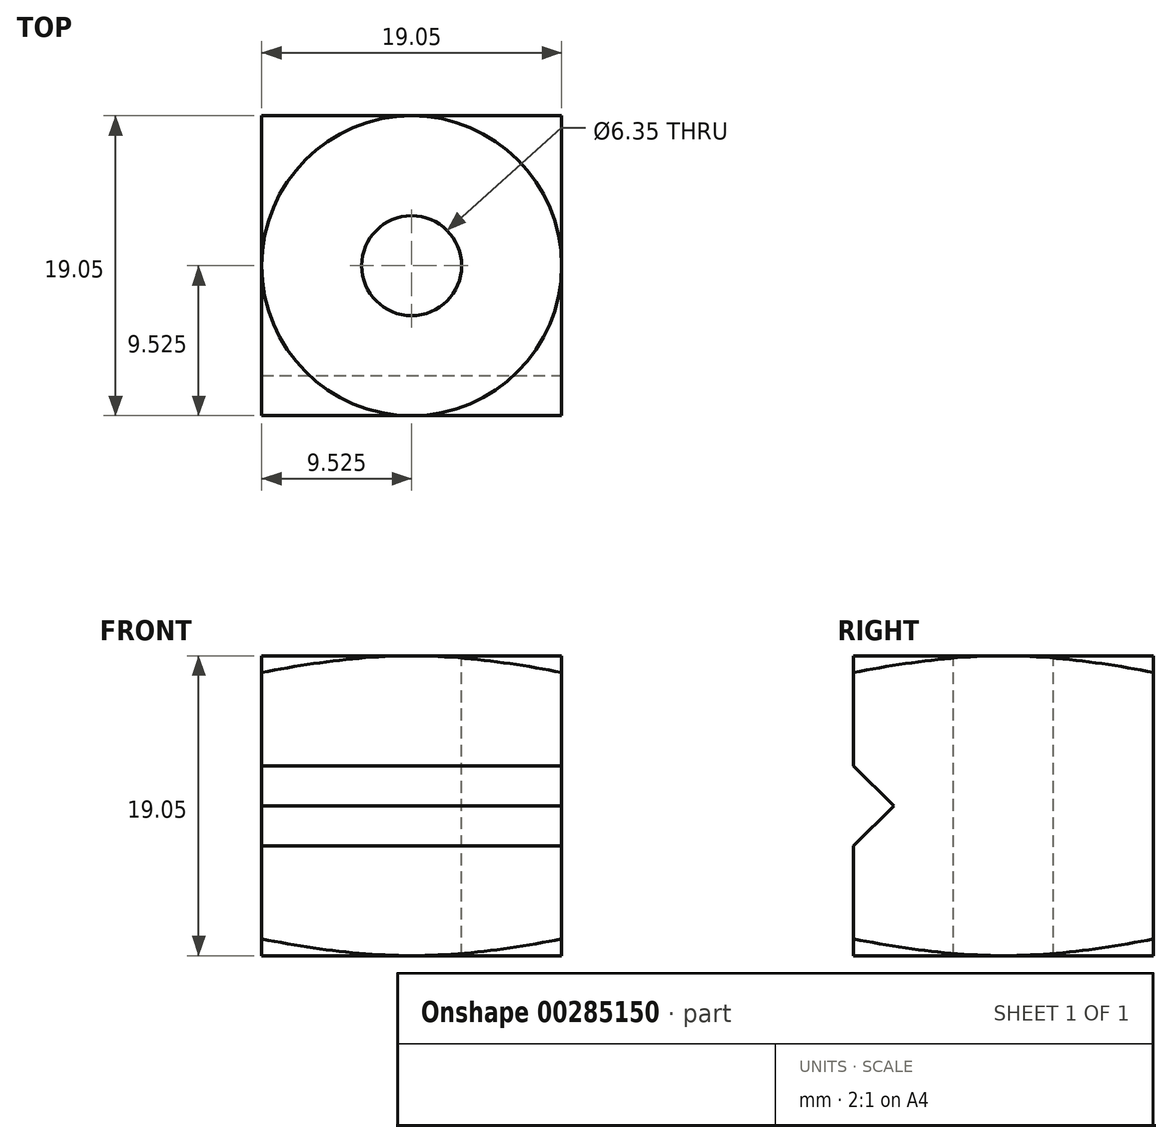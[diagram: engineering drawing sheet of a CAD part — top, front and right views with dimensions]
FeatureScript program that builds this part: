
annotation { "Feature Type Name" : "Feature", "Feature Type Description" : "" }
export const myFeature = defineFeature(function(context is Context, id is Id, definition is map)
    precondition{}
    {
        {
            var Q0;
            Q0=qCreatedBy(makeId("Top.planeOp"),FACE);
            var sketch = newSketch(context, id + "F0", { "sketchPlane" : qUnion([Q0])});
            skLineSegment(sketch, "E0.bottom", {"start": v(0, 0) * mm, "end": v(19.05, 0) * mm});
            skLineSegment(sketch, "E0.top", {"start": v(0, -19.05) * mm, "end": v(19.05, -19.05) * mm});
            skLineSegment(sketch, "E0.left", {"start": v(0, 0) * mm, "end": v(0, -19.05) * mm});
            skLineSegment(sketch, "E0.right", {"start": v(19.05, 0) * mm, "end": v(19.05, -19.05) * mm});
            skSolve(sketch);
        }
        {
            var Q0;
            Q0=makeQuery(id+"F0.imprint","IMPRINT",FACE,{"disambiguationData":[TD([[makeQuery(id+"F0.imprint","IMPRINT",EDGE,{"derivedFrom":sQuery(id+"F0.wireOp",EDGE,"E0.bottom")}),-1.0]])]});
            extrude(context, id + "F1", {"entities" : qUnion([Q0]), "depth" : 19.05 * mm});
        }
        {
            var Q0;
            Q0=makeQuery(id+"F1.opExtrude","CAP_FACE",FACE,{"disambiguationData":[OSD([sQuery(id+"F0.wireOp",EDGE,"E0.bottom"),sQuery(id+"F0.wireOp",EDGE,"E0.top"),sQuery(id+"F0.wireOp",EDGE,"E0.left"),sQuery(id+"F0.wireOp",EDGE,"E0.right")])],"isStart":false});
            var sketch = newSketch(context, id + "F2", { "sketchPlane" : qUnion([Q0])});
            skCircle(sketch, "E1", {"center": v(9.53, -9.53) * mm, "radius": 3.18 * mm});
            skCircle(sketch, "E2", {"center": v(9.53, -9.53) * mm, "radius": 9.53 * mm});
            skSolve(sketch);
        }
        {
            var Q0;
            Q0=makeQuery(id+"F2.imprint","IMPRINT",FACE,{"disambiguationData":[TD([[makeQuery(id+"F2.imprint","IMPRINT",EDGE,{"derivedFrom":sQuery(id+"F2.wireOp",EDGE,"E1")}),1.0]])]});
            extrude(context, id + "F3", {"entities" : qUnion([Q0]), "operationType" : NewBodyOperationType.REMOVE, "endBound" : BoundingType.THROUGH_ALL, "oppositeDirection" : true, "depth" : 25.4 * mm});
        }
        {
            var Q0;
            Q0=makeQuery(id+"F1.opExtrude","CAP_FACE",FACE,{"disambiguationData":[OSD([sQuery(id+"F0.wireOp",EDGE,"E0.bottom"),sQuery(id+"F0.wireOp",EDGE,"E0.top"),sQuery(id+"F0.wireOp",EDGE,"E0.left"),sQuery(id+"F0.wireOp",EDGE,"E0.right")])],"isStart":true});
            var sketch = newSketch(context, id + "F4", { "sketchPlane" : qUnion([Q0])});
            skCircle(sketch, "E3.0", {"center": v(9.53, 9.53) * mm, "radius": 9.53 * mm});
            skSolve(sketch);
        }
        {
            var Q0;
            Q0=makeQuery(id+"F1.opExtrude","SWEPT_FACE",FACE,{"disambiguationData":[OSD([sQuery(id+"F0.wireOp",EDGE,"E0.left")])]});
            cPlane(context, id + "F5", {"entities" : qUnion([Q0]), "cplaneType" : CPlaneType.OFFSET, "offset" : 9.52 * mm, "oppositeDirection" : true, "width" : 152.4 * mm, "height" : 152.4 * mm});
        }
        {
            var Q0;
            Q0=qCreatedBy(id+"F5.planeOp",FACE);
            var sketch = newSketch(context, id + "F6", { "sketchPlane" : qUnion([Q0])});
            skPoint(sketch, "E4.0", {"position": v(19.05, 19.05) * mm});
            skLineSegment(sketch, "E5", {"start": v(19.05, 19.05) * mm, "end": v(34.3, 19.05) * mm});
            skLineSegment(sketch, "E6", {"start": v(34.3, 19.05) * mm, "end": v(34.3, 14.97) * mm});
            skLineSegment(sketch, "E7", {"start": v(34.3, 14.97) * mm, "end": v(19.05, 19.05) * mm});
            skSolve(sketch);
        }
        {
            var Q0;
            Q0=makeQuery(id+"F6.imprint","IMPRINT",FACE,{"disambiguationData":[TD([[makeQuery(id+"F6.imprint","IMPRINT",EDGE,{"derivedFrom":sQuery(id+"F6.wireOp",EDGE,"E5")}),-1.0]])]});
            var Q1;
            Q1=sQuery(id+"F2.wireOp",EDGE,"E2");
            revolve(context, id + "F7", {"operationType" : NewBodyOperationType.REMOVE, "entities" : qUnion([Q0]), "axis" : qUnion([Q1]), "revolveType" : RevolveType.FULL, "oppositeDirection" : true});
        }
        {
            var Q0;
            Q0=qCreatedBy(id+"F5.planeOp",FACE);
            var sketch = newSketch(context, id + "F8", { "sketchPlane" : qUnion([Q0])});
            skLineSegment(sketch, "E8.0", {"start": v(0, 0) * mm, "end": v(19.05, 0) * mm});
            skLineSegment(sketch, "E9", {"start": v(19.05, 0) * mm, "end": v(30.5, 0) * mm});
            skLineSegment(sketch, "E10", {"start": v(30.5, 0) * mm, "end": v(30.5, 3.07) * mm});
            skLineSegment(sketch, "E11", {"start": v(30.5, 3.07) * mm, "end": v(19.05, 0) * mm});
            skSolve(sketch);
        }
        {
            var Q0;
            Q0=makeQuery(id+"F8.imprint","IMPRINT",FACE,{"disambiguationData":[TD([[makeQuery(id+"F8.imprint","IMPRINT",EDGE,{"derivedFrom":sQuery(id+"F8.wireOp",EDGE,"E9")}),1.0]])]});
            var Q1;
            Q1=sQuery(id+"F4.wireOp",EDGE,"E3.0");
            revolve(context, id + "F9", {"operationType" : NewBodyOperationType.REMOVE, "entities" : qUnion([Q0]), "axis" : qUnion([Q1]), "revolveType" : RevolveType.FULL, "oppositeDirection" : true});
        }
        {
            var Q0;
            Q0=makeQuery(id+"F1.opExtrude","SWEPT_FACE",FACE,{"disambiguationData":[OSD([sQuery(id+"F0.wireOp",EDGE,"E0.right")])]});
            var sketch = newSketch(context, id + "F10", { "sketchPlane" : qUnion([Q0])});
            skLineSegment(sketch, "E12", {"start": v(-19.05, 9.53) * mm, "end": v(-16.51, 9.53) * mm});
            skLineSegment(sketch, "E13", {"start": v(-16.51, 9.53) * mm, "end": v(-19.05, 12.07) * mm});
            skLineSegment(sketch, "E14", {"start": v(-16.51, 9.53) * mm, "end": v(-19.05, 6.99) * mm});
            skSolve(sketch);
        }
        {
            var Q0;
            Q0 = qSketchRegion(id + "F10", true);
            var Q1;
            {var subQ0=sQuery(id+"F10.wireOp",EDGE,"E12");Q1=makeQuery(id+"F10.imprint","IMPRINT",FACE,{"disambiguationData":[TD([[makeQuery(id+"F10.imprint","IMPRINT",EDGE,{"derivedFrom":subQ0}),1.0]])]});}
            var Q2;
            {var subQ0=sQuery(id+"F10.wireOp",EDGE,"E12");Q2=makeQuery(id+"F10.imprint","IMPRINT",FACE,{"disambiguationData":[TD([[makeQuery(id+"F10.imprint","IMPRINT",EDGE,{"derivedFrom":subQ0}),-1.0]])]});}
            extrude(context, id + "F11", {"entities" : qUnion([Q0, Q1, Q2]), "operationType" : NewBodyOperationType.REMOVE, "endBound" : BoundingType.THROUGH_ALL, "oppositeDirection" : true, "depth" : 25.4 * mm});
        }
    });
